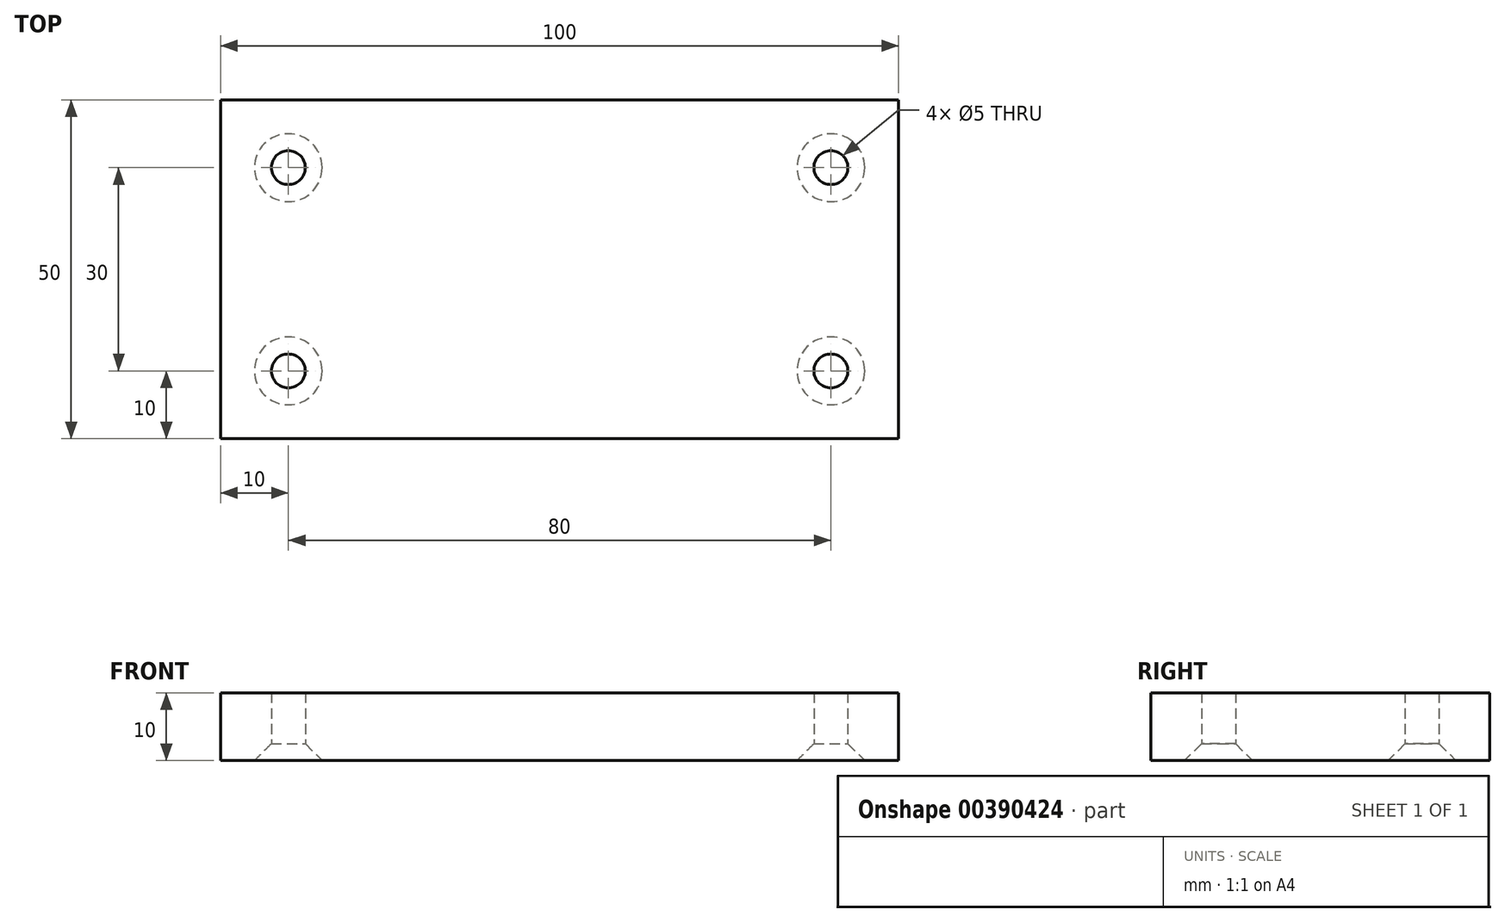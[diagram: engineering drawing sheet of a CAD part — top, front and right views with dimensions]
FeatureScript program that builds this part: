
annotation { "Feature Type Name" : "Feature", "Feature Type Description" : "" }
export const myFeature = defineFeature(function(context is Context, id is Id, definition is map)
    precondition{}
    {
        {
            var Q0;
            Q0=qCreatedBy(makeId("Top.planeOp"),FACE);
            var sketch = newSketch(context, id + "F0", { "sketchPlane" : qUnion([Q0])});
            skLineSegment(sketch, "E0.bottom", {"start": v(50, -25) * mm, "end": v(-50, -25) * mm});
            skLineSegment(sketch, "E0.top", {"start": v(50, 25) * mm, "end": v(-50, 25) * mm});
            skLineSegment(sketch, "E0.left", {"start": v(50, -25) * mm, "end": v(50, 25) * mm});
            skLineSegment(sketch, "E0.right", {"start": v(-50, -25) * mm, "end": v(-50, 25) * mm});
            skPoint(sketch, "E0.middle", {"position": v(0, 0) * mm});
            skPoint(sketch, "E1", {"position": v(-40, 15) * mm});
            skPoint(sketch, "E2.MirrorP", {"position": v(40, 15) * mm});
            skPoint(sketch, "E3.MirrorP", {"position": v(-40, -15) * mm});
            skPoint(sketch, "E4.MirrorP", {"position": v(40, -15) * mm});
            skPoint(sketch, "E5.orphan", {"position": v(0, 25) * mm});
            skPoint(sketch, "E6.end.orphan", {"position": v(0, -25) * mm});
            skSolve(sketch);
        }
        {
            var Q0;
            Q0=makeQuery(id+"F0.imprint","IMPRINT",FACE,{"disambiguationData":[TD([[makeQuery(id+"F0.imprint","IMPRINT",EDGE,{"derivedFrom":sQuery(id+"F0.wireOp",EDGE,"E0.bottom")}),-1.0]])]});
            extrude(context, id + "F1", {"entities" : qUnion([Q0]), "depth" : 10 * mm});
        }
        {
            var Q0;
            Q0=sQuery(id+"F0.wireOp",VERTEX,"E3.MirrorP");
            var Q1;
            Q1=sQuery(id+"F0.wireOp",VERTEX,"E2.MirrorP");
            var Q2;
            Q2=sQuery(id+"F0.wireOp",VERTEX,"E1");
            var Q3;
            Q3=sQuery(id+"F0.wireOp",VERTEX,"E4.MirrorP");
            var Q4;
            Q4=makeQuery(id+"F1.opExtrude","SWEPT_BODY",BODY,{"disambiguationData":[OSD([sQuery(id+"F0.wireOp",EDGE,"E0.bottom"),sQuery(id+"F0.wireOp",EDGE,"E0.top"),sQuery(id+"F0.wireOp",EDGE,"E0.left"),sQuery(id+"F0.wireOp",EDGE,"E0.right")])]});
            hole(context, id + "F2", {"style" : HoleStyle.C_SINK, "endStyle" : HoleEndStyle.THROUGH, "oppositeDirection" : true, "holeDiameter" : 5 * mm, "cSinkDiameter" : 10 * mm, "cSinkAngle" : 90 * degree, "isTappedThrough" : true, "tappedDepth" : 12 * mm, "tapClearance" : 3, "locations" : qUnion([Q0, Q1, Q2, Q3]), "scope" : qUnion([Q4])});
        }
    });
